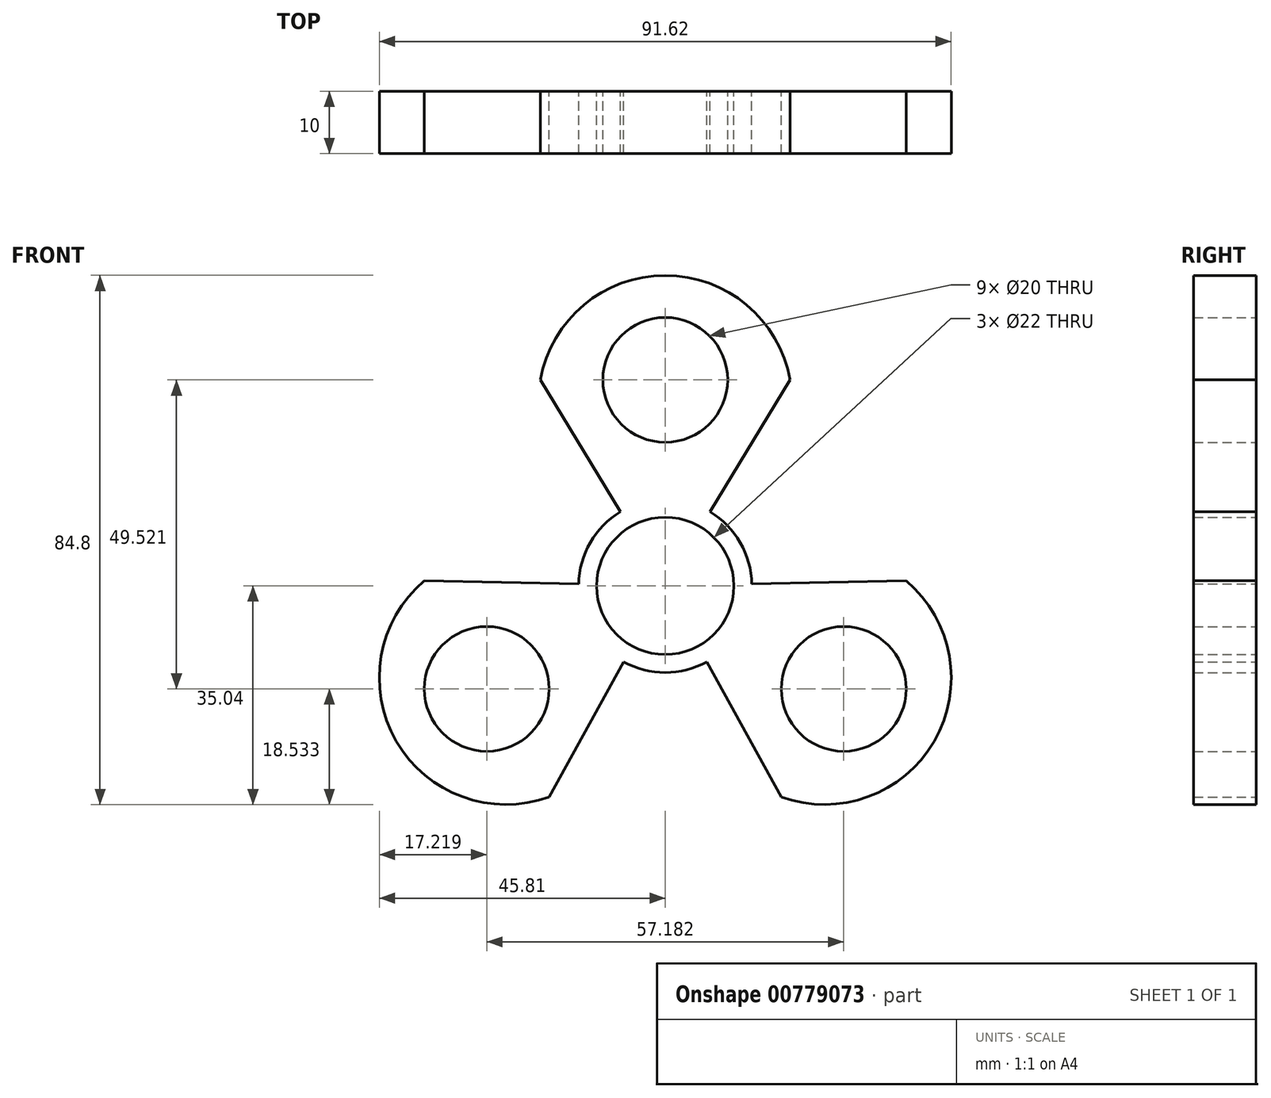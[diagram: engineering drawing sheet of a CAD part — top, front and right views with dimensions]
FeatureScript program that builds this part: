
annotation { "Feature Type Name" : "Feature", "Feature Type Description" : "" }
export const myFeature = defineFeature(function(context is Context, id is Id, definition is map)
    precondition{}
    {
        {
            var Q0;
            Q0=qCreatedBy(makeId("Front.planeOp"),FACE);
            var sketch = newSketch(context, id + "F0", { "sketchPlane" : qUnion([Q0])});
            skArc(sketch, "E0", {"start": v(9.53, 5.5) * mm, "mid": v(0, 11) * mm, "end": v(-9.53, 5.5) * mm});
            skArc(sketch, "E1", {"start": v(-7.19, 11.87) * mm, "mid": v(-9.91, 9.7) * mm, "end": v(-12.02, 6.94) * mm});
            skCircle(sketch, "E2", {"center": v(0, 33.01) * mm, "radius": 10 * mm});
            skArc(sketch, "E3", {"start": v(20, 33.01) * mm, "mid": v(0, 49.76) * mm, "end": v(-20, 33.01) * mm});
            skLineSegment(sketch, "E4", {"start": v(-20, 33.01) * mm, "end": v(-7.19, 11.87) * mm});
            skLineSegment(sketch, "E5", {"start": v(20, 33.01) * mm, "end": v(7.19, 11.87) * mm});
            skLineSegment(sketch, "E6.trimOffspring", {"start": v(0, 49.76) * mm, "end": v(0, 50) * mm});
            skArc(sketch, "E7.trimOffspring", {"start": v(12.02, 6.94) * mm, "mid": v(9.91, 9.7) * mm, "end": v(7.19, 11.87) * mm});
            skLineSegment(sketch, "E8.1.0", {"start": v(-38.6, 0.81) * mm, "end": v(-13.87, 0.3) * mm});
            skLineSegment(sketch, "E8.1.1", {"start": v(-18.6, -33.83) * mm, "end": v(-6.68, -12.16) * mm});
            skArc(sketch, "E8.1.2", {"start": v(-38.6, 0.81) * mm, "mid": v(-43.1, -24.88) * mm, "end": v(-18.6, -33.83) * mm});
            skCircle(sketch, "E8.1.3", {"center": v(-28.6, -16.5) * mm, "radius": 10 * mm});
            skArc(sketch, "E8.1.4", {"start": v(-9.53, 5.5) * mm, "mid": v(-9.53, -5.5) * mm, "end": v(0, -11) * mm});
            skArc(sketch, "E8.1.5", {"start": v(-12.02, 6.94) * mm, "mid": v(-13.36, 3.73) * mm, "end": v(-13.87, 0.3) * mm});
            skLineSegment(sketch, "E8.1.6", {"start": v(-43.1, -24.88) * mm, "end": v(-43.3, -25) * mm});
            skArc(sketch, "E8.1.7", {"start": v(-6.68, -12.16) * mm, "mid": v(-3.45, -13.44) * mm, "end": v(0, -13.88) * mm});
            skLineSegment(sketch, "E8.2.0", {"start": v(18.6, -33.83) * mm, "end": v(6.68, -12.16) * mm});
            skLineSegment(sketch, "E8.2.1", {"start": v(38.6, 0.81) * mm, "end": v(13.87, 0.3) * mm});
            skArc(sketch, "E8.2.2", {"start": v(18.6, -33.83) * mm, "mid": v(43.1, -24.88) * mm, "end": v(38.6, 0.81) * mm});
            skCircle(sketch, "E8.2.3", {"center": v(28.6, -16.5) * mm, "radius": 10 * mm});
            skArc(sketch, "E8.2.4", {"start": v(0, -11) * mm, "mid": v(9.53, -5.5) * mm, "end": v(9.53, 5.5) * mm});
            skArc(sketch, "E8.2.5", {"start": v(0, -13.88) * mm, "mid": v(3.45, -13.44) * mm, "end": v(6.68, -12.16) * mm});
            skLineSegment(sketch, "E8.2.6", {"start": v(43.1, -24.88) * mm, "end": v(43.3, -25) * mm});
            skArc(sketch, "E8.2.7", {"start": v(13.87, 0.3) * mm, "mid": v(13.36, 3.73) * mm, "end": v(12.02, 6.94) * mm});
            skSolve(sketch);
        }
        {
            var Q0;
            Q0=makeQuery(id+"F0.imprint","IMPRINT",FACE,{"disambiguationData":[TD([[makeQuery(id+"F0.imprint","IMPRINT",EDGE,{"derivedFrom":sQuery(id+"F0.wireOp",EDGE,"E0")}),-1.0]])]});
            extrude(context, id + "F1", {"entities" : qUnion([Q0]), "depth" : 10 * mm, "offsetDistance" : 25 * mm});
        }
    });
